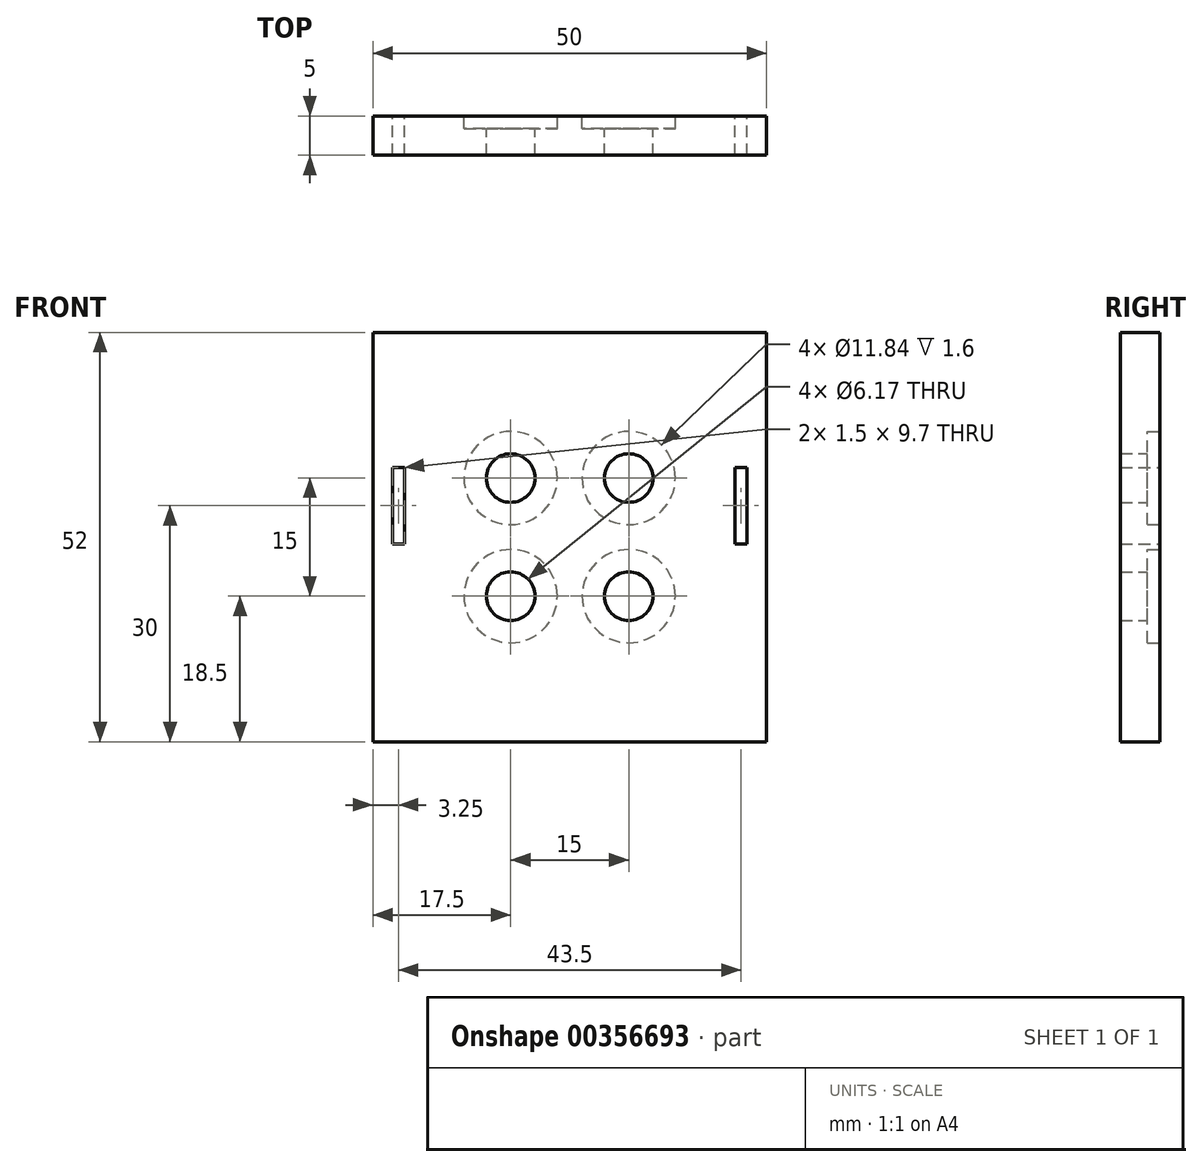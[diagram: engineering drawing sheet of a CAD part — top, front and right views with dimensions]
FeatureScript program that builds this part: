
annotation { "Feature Type Name" : "Feature", "Feature Type Description" : "" }
export const myFeature = defineFeature(function(context is Context, id is Id, definition is map)
    precondition{}
    {
        {
            var Q0;
            Q0=qCreatedBy(makeId("Front.planeOp"),FACE);
            var sketch = newSketch(context, id + "F0", { "sketchPlane" : qUnion([Q0])});
            skLineSegment(sketch, "E0.bottom", {"start": v(25, -26) * mm, "end": v(-25, -26) * mm});
            skLineSegment(sketch, "E0.top", {"start": v(25, 26) * mm, "end": v(-25, 26) * mm});
            skLineSegment(sketch, "E0.left", {"start": v(25, -26) * mm, "end": v(25, 26) * mm});
            skLineSegment(sketch, "E0.right", {"start": v(-25, -26) * mm, "end": v(-25, 26) * mm});
            skPoint(sketch, "E0.middle", {"position": v(0, 0) * mm});
            skLineSegment(sketch, "E1.bottom", {"start": v(-22.5, 8.85) * mm, "end": v(-21, 8.85) * mm});
            skLineSegment(sketch, "E1.top", {"start": v(-22.5, -0.85) * mm, "end": v(-21, -0.85) * mm});
            skLineSegment(sketch, "E1.left", {"start": v(-22.5, 8.85) * mm, "end": v(-22.5, -0.85) * mm});
            skLineSegment(sketch, "E1.right", {"start": v(-21, 8.85) * mm, "end": v(-21, -0.85) * mm});
            skLineSegment(sketch, "E2.bottom", {"start": v(21, 8.85) * mm, "end": v(22.5, 8.85) * mm});
            skLineSegment(sketch, "E2.top", {"start": v(21, -0.85) * mm, "end": v(22.5, -0.85) * mm});
            skLineSegment(sketch, "E2.left", {"start": v(21, 8.85) * mm, "end": v(21, -0.85) * mm});
            skLineSegment(sketch, "E2.right", {"start": v(22.5, 8.85) * mm, "end": v(22.5, -0.85) * mm});
            skSolve(sketch);
        }
        {
            var Q0;
            Q0=qSketchRegion(id+"F0",true);
            extrude(context, id + "F1", {"entities" : qUnion([Q0]), "depth" : 5 * mm});
        }
        {
            var Q0;
            Q0=qCreatedBy(makeId("Front.planeOp"),FACE);
            var sketch = newSketch(context, id + "F2", { "sketchPlane" : qUnion([Q0])});
            skCircle(sketch, "E3", {"center": v(7.5, 7.5) * mm, "radius": 5.92 * mm});
            skCircle(sketch, "E4", {"center": v(7.5, -7.5) * mm, "radius": 5.92 * mm});
            skCircle(sketch, "E5", {"center": v(-7.5, -7.5) * mm, "radius": 5.92 * mm});
            skCircle(sketch, "E6", {"center": v(-7.5, 7.5) * mm, "radius": 5.92 * mm});
            skSolve(sketch);
        }
        {
            var Q0;
            Q0=qSketchRegion(id+"F2",true);
            extrude(context, id + "F3", {"entities" : qUnion([Q0]), "operationType" : NewBodyOperationType.REMOVE, "depth" : 1.6 * mm});
        }
        {
            var Q0;
            Q0=qCreatedBy(makeId("Front.planeOp"),FACE);
            var sketch = newSketch(context, id + "F4", { "sketchPlane" : qUnion([Q0])});
            skCircle(sketch, "E7", {"center": v(7.5, 7.5) * mm, "radius": 3.09 * mm});
            skCircle(sketch, "E8", {"center": v(-7.5, 7.5) * mm, "radius": 3.09 * mm});
            skCircle(sketch, "E9", {"center": v(-7.5, -7.5) * mm, "radius": 3.09 * mm});
            skCircle(sketch, "E10", {"center": v(7.5, -7.5) * mm, "radius": 3.09 * mm});
            skSolve(sketch);
        }
        {
            var Q0;
            Q0=qSketchRegion(id+"F4",true);
            extrude(context, id + "F5", {"entities" : qUnion([Q0]), "operationType" : NewBodyOperationType.REMOVE, "endBound" : BoundingType.THROUGH_ALL, "depth" : 25 * mm});
        }
    });
